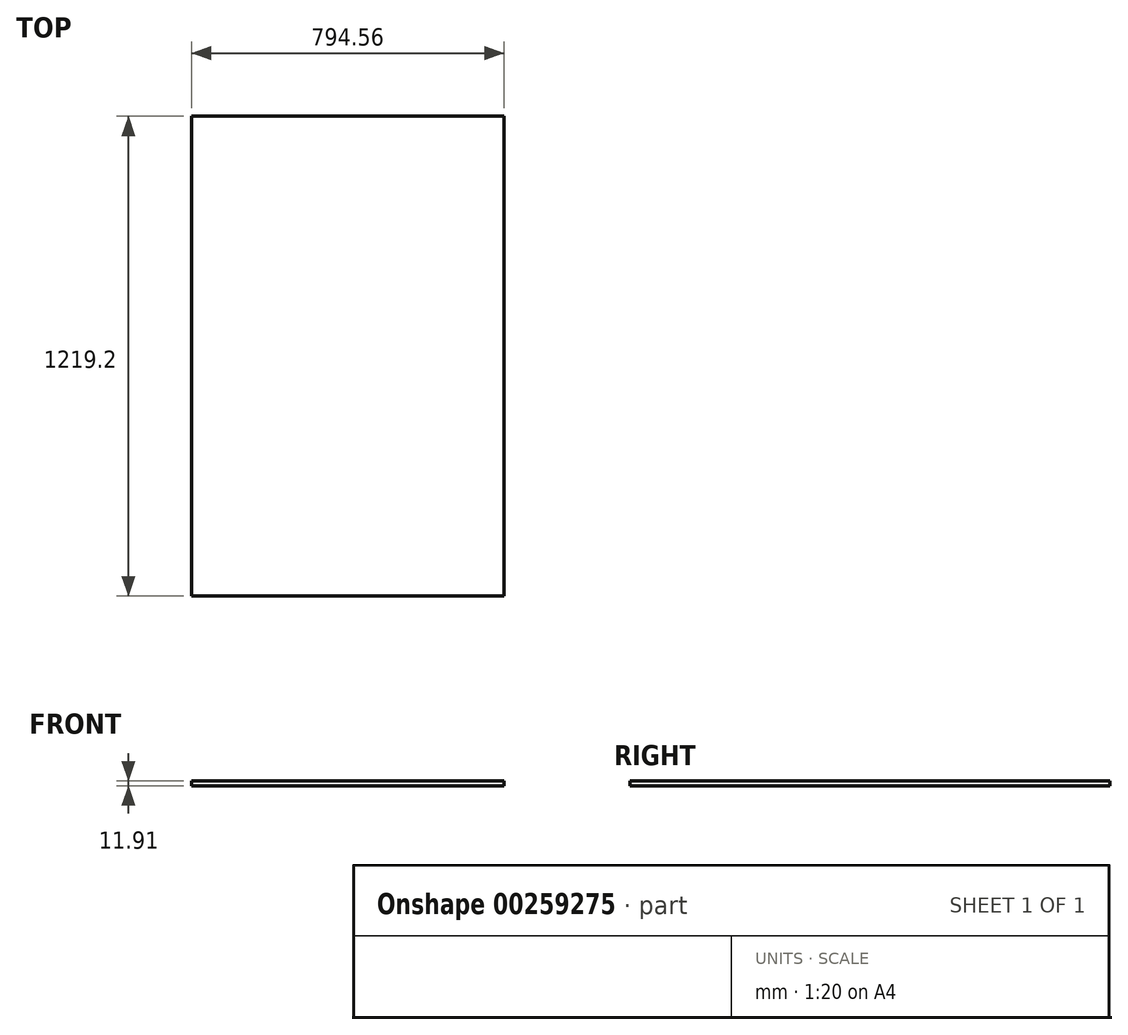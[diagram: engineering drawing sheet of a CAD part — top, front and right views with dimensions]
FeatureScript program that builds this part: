
annotation { "Feature Type Name" : "Feature", "Feature Type Description" : "" }
export const myFeature = defineFeature(function(context is Context, id is Id, definition is map)
    precondition{}
    {
        {
            var Q0;
            Q0=qCreatedBy(makeId("Top.planeOp"),FACE);
            var sketch = newSketch(context, id + "F0", { "sketchPlane" : qUnion([Q0])});
            skLineSegment(sketch, "E0.bottom", {"start": v(-397.28, 609.6) * mm, "end": v(397.28, 609.6) * mm});
            skLineSegment(sketch, "E0.top", {"start": v(-397.28, -609.6) * mm, "end": v(397.28, -609.6) * mm});
            skLineSegment(sketch, "E0.left", {"start": v(-397.28, 609.6) * mm, "end": v(-397.28, -609.6) * mm});
            skLineSegment(sketch, "E0.right", {"start": v(397.28, 609.6) * mm, "end": v(397.28, -609.6) * mm});
            skPoint(sketch, "E0.middle", {"position": v(0, 0) * mm});
            skSolve(sketch);
        }
        {
            var Q0;
            Q0=makeQuery(id+"F0.imprint","IMPRINT",FACE,{"disambiguationData":[TD([[makeQuery(id+"F0.imprint","IMPRINT",EDGE,{"derivedFrom":sQuery(id+"F0.wireOp",EDGE,"E0.bottom")}),-1.0]])]});
            extrude(context, id + "F1", {"entities" : qUnion([Q0]), "depth" : 11.9 * mm});
        }
    });
